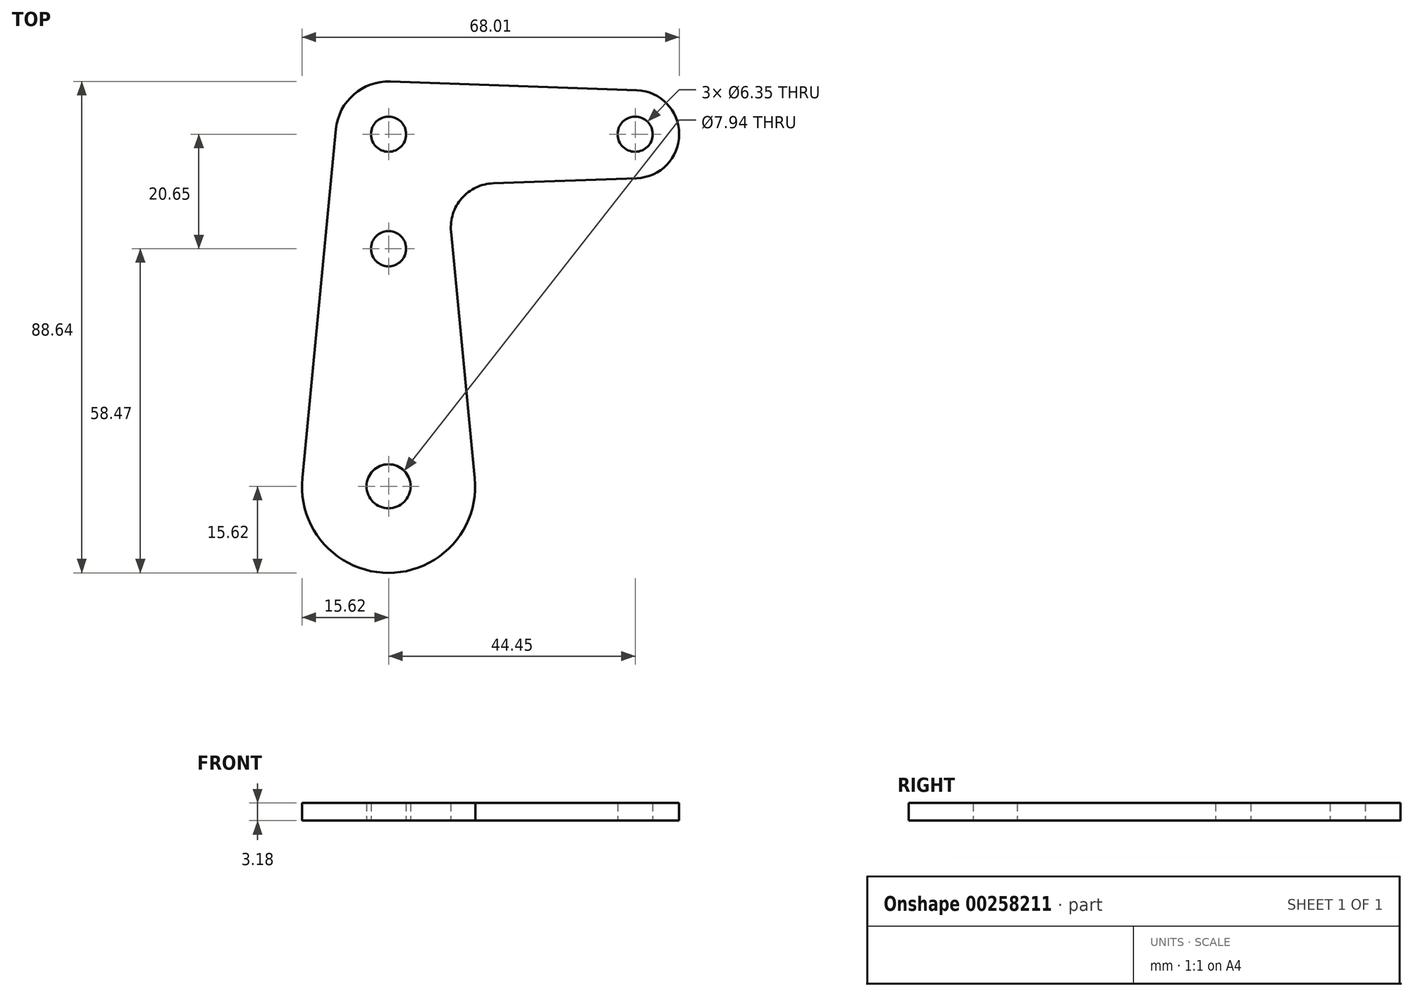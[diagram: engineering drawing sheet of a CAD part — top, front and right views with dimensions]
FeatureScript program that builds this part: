
annotation { "Feature Type Name" : "Feature", "Feature Type Description" : "" }
export const myFeature = defineFeature(function(context is Context, id is Id, definition is map)
    precondition{}
    {
        {
            var Q0;
            Q0=qCreatedBy(makeId("Top.planeOp"),FACE);
            var sketch = newSketch(context, id + "F0", { "sketchPlane" : qUnion([Q0])});
            skLineSegment(sketch, "E0", {"start": v(0, 0) * mm, "end": v(-44.45, 0) * mm, "construction": true});
            skLineSegment(sketch, "E1", {"start": v(-44.45, 0) * mm, "end": v(-44.45, -20.65) * mm, "construction": true});
            skLineSegment(sketch, "E2", {"start": v(-44.45, -20.65) * mm, "end": v(-44.45, -63.5) * mm, "construction": true});
            skCircle(sketch, "E3", {"center": v(0, 0) * mm, "radius": 3.18 * mm});
            skCircle(sketch, "E4", {"center": v(-44.45, 0) * mm, "radius": 3.18 * mm});
            skCircle(sketch, "E5", {"center": v(-44.45, -20.65) * mm, "radius": 3.18 * mm});
            skCircle(sketch, "E6", {"center": v(-44.45, -63.5) * mm, "radius": 3.97 * mm});
            skCircle(sketch, "E7", {"center": v(0, 0) * mm, "radius": 7.94 * mm});
            skCircle(sketch, "E8", {"center": v(-44.45, 0) * mm, "radius": 9.53 * mm});
            skCircle(sketch, "E9", {"center": v(-44.45, -63.5) * mm, "radius": 15.62 * mm});
            skLineSegment(sketch, "E10", {"start": v(-53.93, 0.91) * mm, "end": v(-60, -62) * mm});
            skLineSegment(sketch, "E11", {"start": v(-44.1, 9.52) * mm, "end": v(0.28, 7.93) * mm});
            skLineSegment(sketch, "E12", {"start": v(-44.45, -9.53) * mm, "end": v(0.28, -7.93) * mm});
            skLineSegment(sketch, "E13", {"start": v(-34.97, 0.91) * mm, "end": v(-28.9, -62) * mm});
            skSolve(sketch);
        }
        {
            var Q0;
            Q0 = qSketchRegion(id + "F0", true);
            extrude(context, id + "F1", {"entities" : qUnion([Q0]), "depth" : 3.17 * mm});
        }
        {
            var Q0;
            Q0=makeQuery(id+"F1.opExtrude","SWEPT_EDGE",EDGE,{"disambiguationData":[OSD([sQuery(id+"F0.wireOp",EDGE,"E12"),sQuery(id+"F0.wireOp",EDGE,"E13")])]});
            fillet(context, id + "F2", {"entities" : qUnion([Q0]), "radius" : 7.94 * mm, "tangentPropagation" : true, "allowEdgeOverflow" : false});
        }
    });
